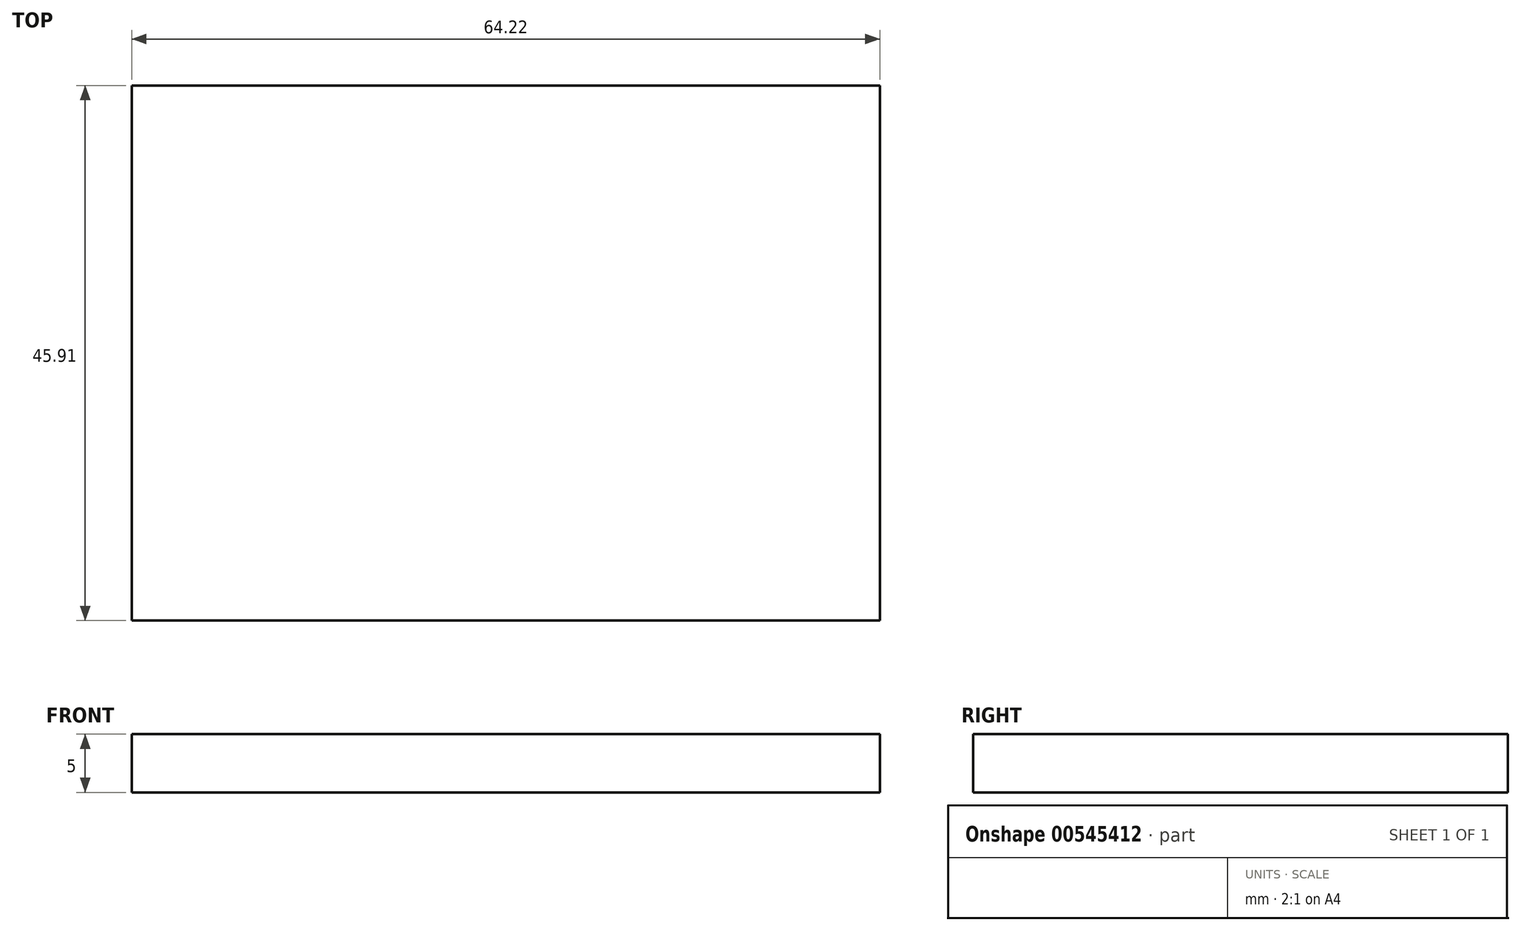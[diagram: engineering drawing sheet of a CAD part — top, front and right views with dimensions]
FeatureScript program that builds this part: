
annotation { "Feature Type Name" : "Feature", "Feature Type Description" : "" }
export const myFeature = defineFeature(function(context is Context, id is Id, definition is map)
    precondition{}
    {
        {
            var Q0;
            Q0=qCreatedBy(makeId("Top.planeOp"),FACE);
            var sketch = newSketch(context, id + "F0", { "sketchPlane" : qUnion([Q0])});
            skLineSegment(sketch, "E0.bottom", {"start": v(-64.22, 45.91) * mm, "end": v(0, 45.91) * mm});
            skLineSegment(sketch, "E0.top", {"start": v(-64.22, 0) * mm, "end": v(0, 0) * mm});
            skLineSegment(sketch, "E0.left", {"start": v(-64.22, 45.91) * mm, "end": v(-64.22, 0) * mm});
            skLineSegment(sketch, "E0.right", {"start": v(0, 45.91) * mm, "end": v(0, 0) * mm});
            skSolve(sketch);
        }
        {
            var Q0;
            Q0=makeQuery(id+"F0.imprint","IMPRINT",FACE,{"disambiguationData":[TD([[makeQuery(id+"F0.imprint","IMPRINT",EDGE,{"derivedFrom":sQuery(id+"F0.wireOp",EDGE,"E0.bottom")}),-1.0]])]});
            extrude(context, id + "F1", {"entities" : qUnion([Q0]), "depth" : 5 * mm, "offsetDistance" : 25 * mm});
        }
    });
